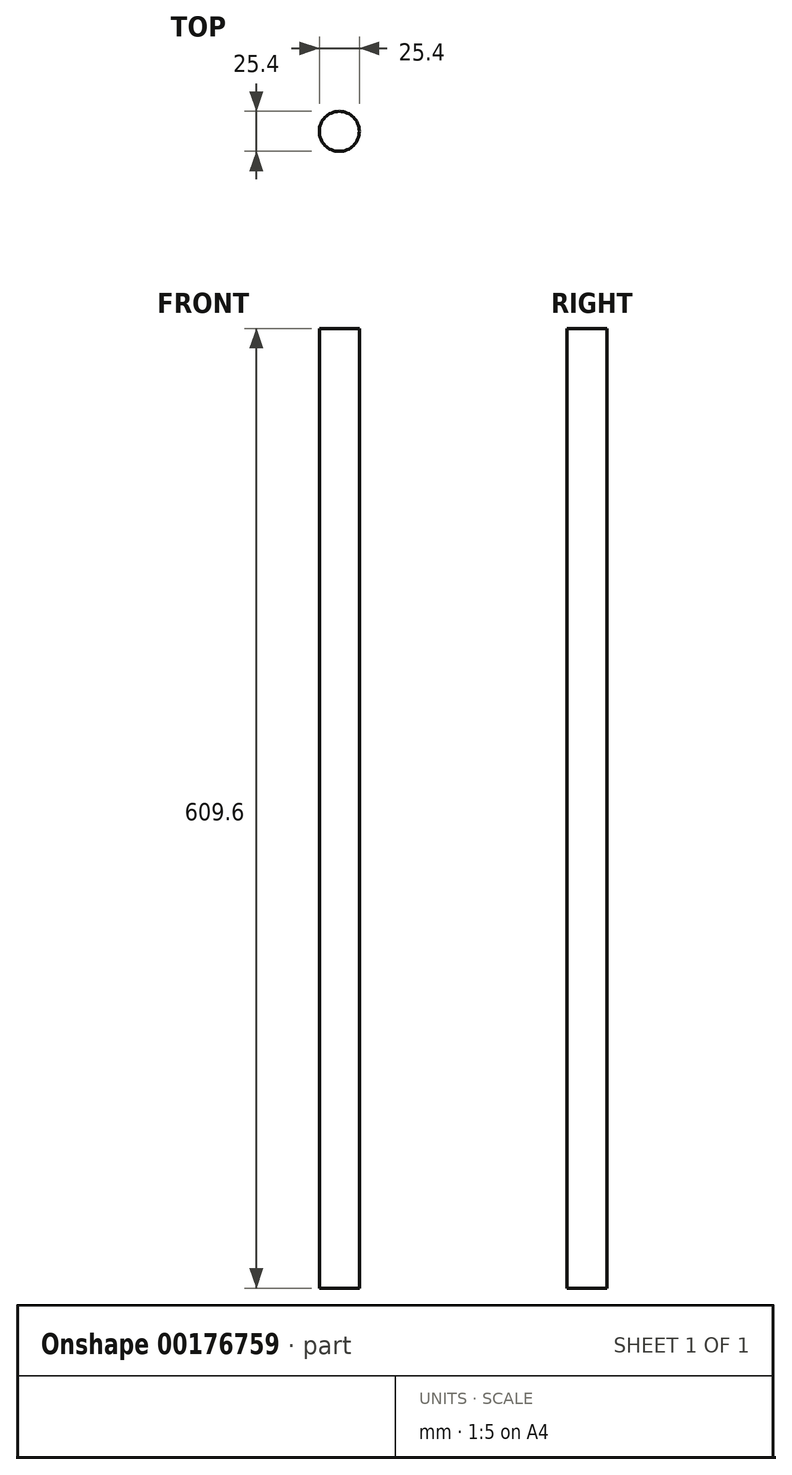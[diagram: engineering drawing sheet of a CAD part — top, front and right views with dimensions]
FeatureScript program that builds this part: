
annotation { "Feature Type Name" : "Feature", "Feature Type Description" : "" }
export const myFeature = defineFeature(function(context is Context, id is Id, definition is map)
    precondition{}
    {
        {
            var Q0;
            Q0=qCreatedBy(makeId("Top.planeOp"),FACE);
            var sketch = newSketch(context, id + "F0", { "sketchPlane" : qUnion([Q0])});
            skCircle(sketch, "E0", {"center": v(0, 0) * mm, "radius": 12.7 * mm});
            skSolve(sketch);
        }
        {
            var Q0;
            Q0=makeQuery(id+"F0.imprint","IMPRINT",FACE,{"disambiguationData":[TD([[makeQuery(id+"F0.imprint","IMPRINT",EDGE,{"derivedFrom":sQuery(id+"F0.wireOp",EDGE,"E0")}),1.0]])]});
            extrude(context, id + "F1", {"entities" : qUnion([Q0]), "depth" : 609.6 * mm});
        }
    });
